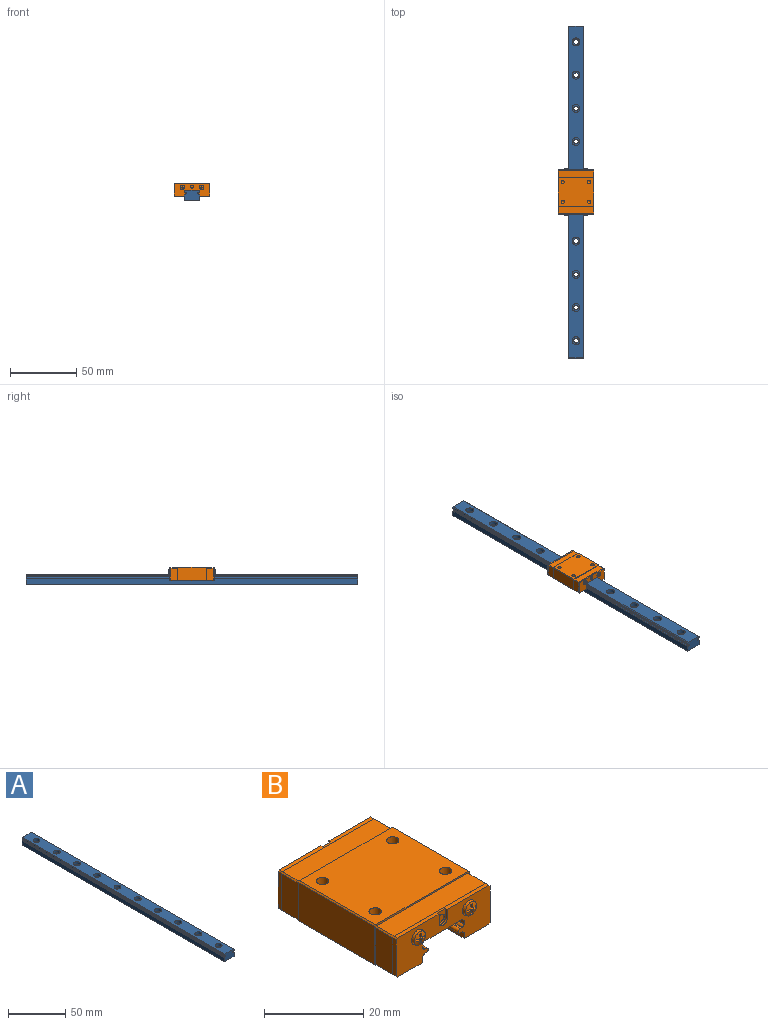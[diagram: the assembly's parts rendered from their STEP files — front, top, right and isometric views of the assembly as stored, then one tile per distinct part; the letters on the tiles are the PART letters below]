
ASSEMBLY  parts=2 mates=1
PART A: 58 faces, bbox 12x250x8 mm
  f0: cylinder r=1.75mm len=5mm, axis (0,0,1), area 55mm2, adj f11,f56
  f1: cylinder r=1.75mm len=5mm, axis (0,0,1), area 55mm2, adj f11,f54
  f2: cylinder r=1.75mm len=5mm, axis (0,0,1), area 55mm2, adj f11,f52
  f3: cylinder r=1.75mm len=5mm, axis (0,0,1), area 55mm2, adj f11,f50
  f4: cylinder r=1.75mm len=5mm, axis (0,0,1), area 55mm2, adj f11,f48
  f5: cylinder r=1.75mm len=5mm, axis (0,0,1), area 55mm2, adj f11,f46
  f6: cylinder r=1.75mm len=5mm, axis (0,0,1), area 55mm2, adj f11,f44
  f7: cylinder r=1.75mm len=5mm, axis (0,0,1), area 55mm2, adj f11,f42
  f8: cylinder r=1.75mm len=5mm, axis (0,0,1), area 55mm2, adj f11,f40
  f9: cylinder r=1.75mm len=5mm, axis (0,0,1), area 55mm2, adj f11,f38
  f10: plane 250x4.32mm, normal (-1,0,0), area 1080.5mm2, adj f11,f26,f27,f37
  f11: plane 250x12mm, normal (0,0,-1), area 2903.8mm2, adj f0,f1,f2,f3,f4,f5,f6,f7
  f12: plane 250x4.32mm, normal (1,0,0), area 1080.5mm2, adj f11,f26,f27,f30
  f13: cylinder r=1.14mm len=250mm, axis (0,1,0), area 156.5mm2, adj f26,f27,f30,f31
  f14: plane 250x0.42mm, normal (0,0,1), area 106.1mm2, adj f15,f26,f27,f31
  f15: cylinder r=0.5mm len=250mm, axis (0,1,0), area 471.3mm2, adj f14,f16,f26,f27
  f16: plane 250x0.42mm, normal (0,0,-1), area 105.2mm2, adj f15,f26,f27,f32
  f17: cylinder r=1.14mm len=250mm, axis (0,1,0), area 156.7mm2, adj f26,f27,f32,f33
  f18: plane 250x0.91mm, normal (1,0,0), area 227.5mm2, adj f26,f27,f29,f33
  f19: plane 250x11mm, normal (0,0,1), area 2467.3mm2, adj f26,f27,f28,f29,f39,f41,f43,f45
  f20: plane 250x0.91mm, normal (-1,0,0), area 227.5mm2, adj f26,f27,f28,f34
  f21: cylinder r=1.14mm len=250mm, axis (0,1,0), area 156.7mm2, adj f26,f27,f34,f35
  f22: plane 250x0.42mm, normal (0,0,-1), area 105.2mm2, adj f23,f26,f27,f35
  f23: cylinder r=0.5mm len=250mm, axis (0,1,0), area 471.3mm2, adj f22,f24,f26,f27
  f24: plane 250x0.42mm, normal (0,0,1), area 106.1mm2, adj f23,f26,f27,f36
  f25: cylinder r=1.14mm len=250mm, axis (0,1,0), area 156.5mm2, adj f26,f27,f36,f37
  f26: plane 12x8mm, normal (0,-1,0), area 91.8mm2, adj f10,f11,f12,f13,f14,f15,f16,f17
  f27: plane 12x8mm, normal (0,1,0), area 91.8mm2, adj f10,f11,f12,f13,f14,f15,f16,f17
  f28: plane 250x0.5mm, normal (-0.71,0,0.71), area 176.8mm2, adj f19,f20,f26,f27
  f29: plane 250x0.5mm, normal (0.71,0,0.71), area 176.8mm2, adj f18,f19,f26,f27
  f30: cylinder r=0.16mm len=250mm, axis (0,1,0), area 42.4mm2, adj f12,f13,f26,f27
  f31: cylinder r=0.16mm len=250mm, axis (0,1,0), area 42.4mm2, adj f13,f14,f26,f27
  f32: cylinder r=0.16mm len=250mm, axis (0,1,0), area 42.4mm2, adj f16,f17,f26,f27
  f33: cylinder r=0.16mm len=250mm, axis (0,1,0), area 42.4mm2, adj f17,f18,f26,f27
  f34: cylinder r=0.16mm len=250mm, axis (0,1,0), area 42.4mm2, adj f20,f21,f26,f27
  f35: cylinder r=0.16mm len=250mm, axis (0,1,0), area 42.4mm2, adj f21,f22,f26,f27
  f36: cylinder r=0.16mm len=250mm, axis (0,1,0), area 42.4mm2, adj f24,f25,f26,f27
  f37: cylinder r=0.16mm len=250mm, axis (0,1,0), area 42.4mm2, adj f10,f25,f26,f27
  f38: plane 6x6mm, normal (0,0,1), area 18.7mm2, adj f9,f39
  f39: cylinder r=3mm len=6mm, axis (0,0,1), area 56.5mm2, adj f19,f38
  f40: plane 6x6mm, normal (0,0,1), area 18.7mm2, adj f8,f41
  f41: cylinder r=3mm len=6mm, axis (0,0,1), area 56.5mm2, adj f19,f40
  f42: plane 6x6mm, normal (0,0,1), area 18.7mm2, adj f7,f43
  f43: cylinder r=3mm len=6mm, axis (0,0,1), area 56.5mm2, adj f19,f42
  f44: plane 6x6mm, normal (0,0,1), area 18.7mm2, adj f6,f45
  f45: cylinder r=3mm len=6mm, axis (0,0,1), area 56.5mm2, adj f19,f44
  f46: plane 6x6mm, normal (0,0,1), area 18.7mm2, adj f5,f47
  f47: cylinder r=3mm len=6mm, axis (0,0,1), area 56.5mm2, adj f19,f46
  f48: plane 6x6mm, normal (0,0,1), area 18.7mm2, adj f4,f49
  f49: cylinder r=3mm len=6mm, axis (0,0,1), area 56.5mm2, adj f19,f48
  f50: plane 6x6mm, normal (0,0,1), area 18.7mm2, adj f3,f51
  f51: cylinder r=3mm len=6mm, axis (0,0,1), area 56.5mm2, adj f19,f50
  f52: plane 6x6mm, normal (0,0,1), area 18.7mm2, adj f2,f53
  f53: cylinder r=3mm len=6mm, axis (0,0,1), area 56.5mm2, adj f19,f52
  f54: plane 6x6mm, normal (0,0,1), area 18.7mm2, adj f1,f55
  f55: cylinder r=3mm len=6mm, axis (0,0,1), area 56.5mm2, adj f19,f54
  f56: plane 6x6mm, normal (0,0,1), area 18.7mm2, adj f0,f57
  f57: cylinder r=3mm len=6mm, axis (0,0,1), area 56.5mm2, adj f19,f56
PART B: 172 faces, bbox 27x35.9x10 mm
  f0: cylinder r=1.25mm len=3.5mm, axis (0,0,-1), area 27.5mm2, adj f1,f158
  f1: cone r=0.62mm half-angle=59deg, axis (0,0,1), area 5.7mm2, adj f0
  f2: cylinder r=1.25mm len=3.5mm, axis (0,0,-1), area 27.5mm2, adj f3,f158
  f3: cone r=0.62mm half-angle=59deg, axis (0,0,1), area 5.7mm2, adj f2
  f4: cylinder r=1.25mm len=3.5mm, axis (0,0,-1), area 27.5mm2, adj f5,f158
  f5: cone r=0.62mm half-angle=59deg, axis (0,0,1), area 5.7mm2, adj f4
  f6: cylinder r=1.25mm len=3.5mm, axis (0,0,-1), area 27.5mm2, adj f7,f158
  f7: cone r=0.62mm half-angle=59deg, axis (0,0,1), area 5.7mm2, adj f6
  f8: cylinder r=0.5mm len=33.7mm, axis (0,1,0), area 63.6mm2, adj f58,f115,f148,f149
  f9: cylinder r=0.5mm len=33.7mm, axis (0,1,0), area 63.6mm2, adj f58,f115,f137,f138
  f10: cylinder r=1.15mm len=2.3mm, axis (0,1,0), area 3.6mm2, adj f114,f124
  f11: cylinder r=1.75mm len=3.5mm, axis (0,1,0), area 5.5mm2, adj f109,f115
  f12: cylinder r=1.75mm len=3.5mm, axis (0,1,0), area 5.5mm2, adj f108,f115
  f13: cone r=0.85mm half-angle=5deg, axis (0,1,0), area 11.5mm2, adj f14,f109
  f14: cone r=0.8mm half-angle=72.7deg, axis (0,1,0), area 6.3mm2, adj f13,f96,f97,f98,f99,f100,f101,f102
  f15: cone r=0.85mm half-angle=5deg, axis (0,1,0), area 11.5mm2, adj f16,f108
  f16: cone r=0.8mm half-angle=72.7deg, axis (0,1,0), area 6.3mm2, adj f15,f83,f84,f85,f86,f87,f88,f89
  f17: cylinder r=1.15mm len=2.3mm, axis (0,-1,0), area 3.6mm2, adj f57,f67
  f18: cylinder r=1.75mm len=3.5mm, axis (0,-1,0), area 5.5mm2, adj f52,f58
  f19: cylinder r=1.75mm len=3.5mm, axis (0,-1,0), area 5.5mm2, adj f51,f58
  f20: cone r=0.85mm half-angle=5deg, axis (0,-1,0), area 11.5mm2, adj f21,f52
  f21: cone r=0.8mm half-angle=72.7deg, axis (0,-1,0), area 6.3mm2, adj f20,f39,f40,f41,f42,f43,f44,f45
  f22: cone r=0.85mm half-angle=5deg, axis (0,-1,0), area 11.5mm2, adj f23,f51
  f23: cone r=0.8mm half-angle=72.7deg, axis (0,-1,0), area 6.3mm2, adj f22,f26,f27,f28,f29,f30,f31,f32
  f24: plane 26.6x9.6mm, normal (0,-1,0), area 0.3mm2, adj f55,f59,f60,f61,f62,f63,f64,f65
  f25: plane 2.4x2.4mm, normal (0,1,0), area 2.1mm2, adj f26,f27,f28,f29,f30,f31,f32,f33
  f26: plane 0.93x0.49mm, normal (0,0,1), area 0.4mm2, adj f23,f25,f29,f31
  f27: plane 0.93x0.49mm, normal (0,0,-1), area 0.4mm2, adj f23,f25,f28,f30
  f28: plane 1.36x1.29mm, normal (-1,0,0), area 1mm2, adj f23,f25,f27,f36
  f29: plane 1.36x1.29mm, normal (-1,0,0), area 1mm2, adj f23,f25,f26,f32
  f30: plane 1.36x1.29mm, normal (1,0,0), area 1mm2, adj f23,f25,f27,f33
  f31: plane 1.36x1.29mm, normal (1,0,0), area 1mm2, adj f23,f25,f26,f34
  f32: plane 1.36x1.29mm, normal (0,0,1), area 1mm2, adj f23,f25,f29,f35
  f33: plane 1.36x1.29mm, normal (0,0,-1), area 1mm2, adj f23,f25,f30,f37
  f34: plane 1.36x1.29mm, normal (0,0,1), area 1mm2, adj f23,f25,f31,f37
  f35: plane 0.93x0.49mm, normal (-1,0,0), area 0.4mm2, adj f23,f25,f32,f36
  f36: plane 1.36x1.29mm, normal (0,0,-1), area 1mm2, adj f23,f25,f28,f35
  f37: plane 0.94x0.49mm, normal (1,0,0), area 0.4mm2, adj f23,f25,f33,f34
  f38: plane 2.4x2.4mm, normal (0,1,0), area 2.1mm2, adj f39,f40,f41,f42,f43,f44,f45,f46
  f39: plane 0.93x0.49mm, normal (0,0,1), area 0.4mm2, adj f21,f38,f42,f44
  f40: plane 0.93x0.49mm, normal (0,0,-1), area 0.4mm2, adj f21,f38,f41,f43
  f41: plane 1.36x1.29mm, normal (-1,0,0), area 1mm2, adj f21,f38,f40,f49
  f42: plane 1.36x1.29mm, normal (-1,0,0), area 1mm2, adj f21,f38,f39,f45
  f43: plane 1.36x1.29mm, normal (1,0,0), area 1mm2, adj f21,f38,f40,f46
  f44: plane 1.36x1.29mm, normal (1,0,0), area 1mm2, adj f21,f38,f39,f47
  f45: plane 1.36x1.29mm, normal (0,0,1), area 1mm2, adj f21,f38,f42,f48
  f46: plane 1.36x1.29mm, normal (0,0,-1), area 1mm2, adj f21,f38,f43,f50
  f47: plane 1.36x1.29mm, normal (0,0,1), area 1mm2, adj f21,f38,f44,f50
  f48: plane 0.93x0.49mm, normal (-1,0,0), area 0.4mm2, adj f21,f38,f45,f49
  f49: plane 1.36x1.29mm, normal (0,0,-1), area 1mm2, adj f21,f38,f41,f48
  f50: plane 0.94x0.49mm, normal (1,0,0), area 0.4mm2, adj f21,f38,f46,f47
  f51: plane 3.5x3.5mm, normal (0,1,0), area 0.5mm2, adj f19,f22
  f52: plane 3.5x3.5mm, normal (0,1,0), area 0.5mm2, adj f18,f20
  f53: plane 2.1x0.5mm, normal (1,0,0), area 1.1mm2, adj f55,f56,f57,f58
  f54: plane 2.1x0.5mm, normal (-1,0,0), area 1.1mm2, adj f55,f56,f57,f58
  f55: plane 26x1mm, normal (0,0,1), area 24.8mm2, adj f24,f53,f54,f57,f58,f62,f63
  f56: cylinder r=1.2mm len=2.4mm, axis (0,-1,0), area 1.9mm2, adj f53,f54,f57,f58
  f57: plane 3.3x2.4mm, normal (0,1,0), area 3.1mm2, adj f17,f53,f54,f55,f56
  f58: plane 26.6x9.6mm, normal (0,1,0), area 172.9mm2, adj f8,f9,f18,f19,f53,f54,f55,f56
  f59: plane 7x1mm, normal (0,0,-1), area 7mm2, adj f24,f58,f65,f134
  f60: plane 7x1mm, normal (0,0,-1), area 7mm2, adj f24,f58,f66,f152
  f61: plane 9x1mm, normal (1,0,0), area 9mm2, adj f24,f58,f62,f66
  f62: plane 1x0.3mm, normal (0.71,0,0.71), area 0.4mm2, adj f24,f55,f58,f61
  f63: plane 1x0.3mm, normal (-0.71,0,0.71), area 0.4mm2, adj f24,f55,f58,f64
  f64: plane 9x1mm, normal (-1,0,0), area 9mm2, adj f24,f58,f63,f65
  f65: plane 1x0.3mm, normal (-0.71,0,-0.71), area 0.4mm2, adj f24,f58,f59,f64
  f66: plane 1x0.3mm, normal (0.71,0,-0.71), area 0.4mm2, adj f24,f58,f60,f61
  f67: plane 2.3x2.3mm, normal (0,1,0), area 4.2mm2, adj f17
  f68: cylinder r=1.14mm len=33.7mm, axis (0,-1,0), area 21.1mm2, adj f58,f115,f150,f151
  f69: cylinder r=1.14mm len=33.7mm, axis (0,-1,0), area 21.1mm2, adj f58,f115,f146,f147
  f70: cylinder r=1.14mm len=33.7mm, axis (0,-1,0), area 21.1mm2, adj f58,f115,f139,f140
  f71: cylinder r=1.14mm len=33.7mm, axis (0,-1,0), area 21.1mm2, adj f58,f115,f135,f136
  f72: plane 7x5mm, normal (0,0,-1), area 35mm2, adj f24,f79,f134,f163
  f73: plane 7x5mm, normal (0,0,-1), area 35mm2, adj f24,f80,f152,f163
  f74: plane 8.99x5mm, normal (1,0,0), area 45mm2, adj f24,f75,f80,f163
  f75: plane 5x0.3mm, normal (0.71,0,0.71), area 2.1mm2, adj f24,f74,f76,f163
  f76: plane 25.99x5mm, normal (0,0,1), area 130mm2, adj f24,f75,f77,f163
  f77: plane 5x0.3mm, normal (-0.71,0,0.71), area 2.1mm2, adj f24,f76,f78,f163
  f78: plane 8.99x5mm, normal (-1,0,0), area 45mm2, adj f24,f77,f79,f163
  f79: plane 5x0.3mm, normal (-0.71,0,-0.71), area 2.1mm2, adj f24,f72,f78,f163
  f80: plane 5x0.3mm, normal (0.71,0,-0.71), area 2.1mm2, adj f24,f73,f74,f163
  f81: plane 26.6x9.6mm, normal (0,1,0), area 0.3mm2, adj f112,f116,f117,f118,f119,f120,f121,f122
  f82: plane 2.4x2.4mm, normal (0,-1,0), area 2.1mm2, adj f83,f84,f85,f86,f87,f88,f89,f90
  f83: plane 0.93x0.49mm, normal (0,0,1), area 0.4mm2, adj f16,f82,f86,f88
  f84: plane 0.93x0.49mm, normal (0,0,-1), area 0.4mm2, adj f16,f82,f85,f87
  f85: plane 1.36x1.29mm, normal (1,0,0), area 1mm2, adj f16,f82,f84,f93
  f86: plane 1.36x1.29mm, normal (1,0,0), area 1mm2, adj f16,f82,f83,f89
  f87: plane 1.36x1.29mm, normal (-1,0,0), area 1mm2, adj f16,f82,f84,f90
  f88: plane 1.36x1.29mm, normal (-1,0,0), area 1mm2, adj f16,f82,f83,f91
  f89: plane 1.36x1.29mm, normal (0,0,1), area 1mm2, adj f16,f82,f86,f92
  f90: plane 1.36x1.29mm, normal (0,0,-1), area 1mm2, adj f16,f82,f87,f94
  f91: plane 1.36x1.29mm, normal (0,0,1), area 1mm2, adj f16,f82,f88,f94
  f92: plane 0.93x0.49mm, normal (1,0,0), area 0.4mm2, adj f16,f82,f89,f93
  f93: plane 1.36x1.29mm, normal (0,0,-1), area 1mm2, adj f16,f82,f85,f92
  f94: plane 0.94x0.49mm, normal (-1,0,0), area 0.4mm2, adj f16,f82,f90,f91
  f95: plane 2.4x2.4mm, normal (0,-1,0), area 2.1mm2, adj f96,f97,f98,f99,f100,f101,f102,f103
  f96: plane 0.93x0.49mm, normal (0,0,1), area 0.4mm2, adj f14,f95,f99,f101
  f97: plane 0.93x0.49mm, normal (0,0,-1), area 0.4mm2, adj f14,f95,f98,f100
  f98: plane 1.36x1.29mm, normal (1,0,0), area 1mm2, adj f14,f95,f97,f106
  f99: plane 1.36x1.29mm, normal (1,0,0), area 1mm2, adj f14,f95,f96,f102
  f100: plane 1.36x1.29mm, normal (-1,0,0), area 1mm2, adj f14,f95,f97,f103
  f101: plane 1.36x1.29mm, normal (-1,0,0), area 1mm2, adj f14,f95,f96,f104
  f102: plane 1.36x1.29mm, normal (0,0,1), area 1mm2, adj f14,f95,f99,f105
  f103: plane 1.36x1.29mm, normal (0,0,-1), area 1mm2, adj f14,f95,f100,f107
  f104: plane 1.36x1.29mm, normal (0,0,1), area 1mm2, adj f14,f95,f101,f107
  f105: plane 0.93x0.49mm, normal (1,0,0), area 0.4mm2, adj f14,f95,f102,f106
  f106: plane 1.36x1.29mm, normal (0,0,-1), area 1mm2, adj f14,f95,f98,f105
  f107: plane 0.94x0.49mm, normal (-1,0,0), area 0.4mm2, adj f14,f95,f103,f104
  f108: plane 3.5x3.5mm, normal (0,-1,0), area 0.5mm2, adj f12,f15
  f109: plane 3.5x3.5mm, normal (0,-1,0), area 0.5mm2, adj f11,f13
  f110: plane 2.1x0.5mm, normal (-1,0,0), area 1mm2, adj f112,f113,f114,f115
  f111: plane 2.1x0.5mm, normal (1,0,0), area 1mm2, adj f112,f113,f114,f115
  f112: plane 26x1mm, normal (0,0,1), area 24.8mm2, adj f81,f110,f111,f114,f115,f119,f120
  f113: cylinder r=1.2mm len=2.4mm, axis (0,1,0), area 1.9mm2, adj f110,f111,f114,f115
  f114: plane 3.3x2.4mm, normal (0,-1,0), area 3.1mm2, adj f10,f110,f111,f112,f113
  f115: plane 26.6x9.6mm, normal (0,-1,0), area 172.9mm2, adj f8,f9,f11,f12,f68,f69,f70,f71
  f116: plane 7x1mm, normal (0,0,-1), area 7mm2, adj f81,f115,f122,f152
  f117: plane 7x1mm, normal (0,0,-1), area 7mm2, adj f81,f115,f123,f134
  f118: plane 9x1mm, normal (-1,0,0), area 9mm2, adj f81,f115,f119,f123
  f119: plane 1x0.3mm, normal (-0.71,0,0.71), area 0.4mm2, adj f81,f112,f115,f118
  f120: plane 1x0.3mm, normal (0.71,0,0.71), area 0.4mm2, adj f81,f112,f115,f121
  f121: plane 9x1mm, normal (1,0,0), area 9mm2, adj f81,f115,f120,f122
  f122: plane 1x0.3mm, normal (0.71,0,-0.71), area 0.4mm2, adj f81,f115,f116,f121
  f123: plane 1x0.3mm, normal (-0.71,0,-0.71), area 0.4mm2, adj f81,f115,f117,f118
  f124: plane 2.3x2.3mm, normal (0,-1,0), area 4.2mm2, adj f10
  f125: plane 7x5mm, normal (0,0,-1), area 35mm2, adj f81,f132,f152,f153
  f126: plane 7x5mm, normal (0,0,-1), area 35mm2, adj f81,f133,f134,f153
  f127: plane 8.99x5mm, normal (-1,0,0), area 44.9mm2, adj f81,f128,f133,f153
  f128: plane 5x0.3mm, normal (-0.71,0,0.71), area 2.1mm2, adj f81,f127,f129,f153
  f129: plane 25.99x5mm, normal (0,0,1), area 129.9mm2, adj f81,f128,f130,f153
  f130: plane 5x0.3mm, normal (0.71,0,0.71), area 2.1mm2, adj f81,f129,f131,f153
  f131: plane 8.99x5mm, normal (1,0,0), area 45mm2, adj f81,f130,f132,f153
  f132: plane 5x0.3mm, normal (0.71,0,-0.71), area 2.1mm2, adj f81,f125,f131,f153
  f133: plane 5x0.3mm, normal (-0.71,0,-0.71), area 2.1mm2, adj f81,f126,f127,f153
  f134: plane 33.7x1.32mm, normal (1,0,0), area 44.5mm2, adj f24,f58,f59,f72,f81,f115,f117,f126
  f135: cylinder r=0.16mm len=33.7mm, axis (0,1,0), area 5.7mm2, adj f58,f71,f115,f134
  f136: cylinder r=0.16mm len=33.7mm, axis (0,1,0), area 5.7mm2, adj f58,f71,f115,f137
  f137: plane 33.7x0.42mm, normal (0,0,-1), area 14.2mm2, adj f9,f58,f115,f136
  f138: plane 33.7x0.42mm, normal (0,0,1), area 14.2mm2, adj f9,f58,f115,f139
  f139: cylinder r=0.16mm len=33.7mm, axis (0,1,0), area 5.7mm2, adj f58,f70,f115,f138
  f140: cylinder r=0.16mm len=33.7mm, axis (0,1,0), area 5.7mm2, adj f58,f70,f115,f141
  f141: plane 33.7x0.82mm, normal (1,0,0), area 27.7mm2, adj f58,f115,f140,f142
  f142: plane 33.7x0.59mm, normal (0.76,0,-0.65), area 26mm2, adj f58,f115,f141,f143
  f143: plane 33.7x11mm, normal (0,0,-1), area 370.7mm2, adj f58,f115,f142,f144
  f144: plane 33.7x0.59mm, normal (-0.76,0,-0.65), area 26mm2, adj f58,f115,f143,f145
  f145: plane 33.7x0.82mm, normal (-1,0,0), area 27.7mm2, adj f58,f115,f144,f146
  f146: cylinder r=0.16mm len=33.7mm, axis (0,1,0), area 5.7mm2, adj f58,f69,f115,f145
  f147: cylinder r=0.16mm len=33.7mm, axis (0,1,0), area 5.7mm2, adj f58,f69,f115,f148
  f148: plane 33.7x0.42mm, normal (0,0,1), area 14.2mm2, adj f8,f58,f115,f147
  f149: plane 33.7x0.42mm, normal (0,0,-1), area 14.2mm2, adj f8,f58,f115,f150
  f150: cylinder r=0.16mm len=33.7mm, axis (0,1,0), area 5.7mm2, adj f58,f68,f115,f149
  f151: cylinder r=0.16mm len=33.7mm, axis (0,1,0), area 5.7mm2, adj f58,f68,f115,f152
  f152: plane 33.7x1.32mm, normal (-1,0,0), area 44.5mm2, adj f24,f58,f60,f73,f81,f115,f116,f125
  f153: plane 27x10mm, normal (0,-1,0), area 14.9mm2, adj f125,f126,f127,f128,f129,f130,f131,f132
  f154: plane 21.7x7.2mm, normal (0,0,-1), area 156.2mm2, adj f152,f153,f161,f163
  f155: plane 21.7x7.2mm, normal (0,0,-1), area 156.2mm2, adj f134,f153,f162,f163
  f156: plane 21.7x9.4mm, normal (-1,0,0), area 204mm2, adj f153,f157,f162,f163
  f157: plane 21.7x0.3mm, normal (-0.71,0,0.71), area 9.2mm2, adj f153,f156,f158,f163
  f158: plane 26.4x21.7mm, normal (0,0,1), area 553.2mm2, adj f0,f2,f4,f6,f153,f157,f159,f163
  f159: plane 21.7x0.3mm, normal (0.71,0,0.71), area 9.2mm2, adj f153,f158,f160,f163
  f160: plane 21.7x9.4mm, normal (1,0,0), area 204mm2, adj f153,f159,f161,f163
  f161: plane 21.7x0.3mm, normal (0.71,0,-0.71), area 9.2mm2, adj f153,f154,f160,f163
  f162: plane 21.7x0.3mm, normal (-0.71,0,-0.71), area 9.2mm2, adj f153,f155,f156,f163
  f163: plane 27x10mm, normal (0,1,0), area 14.9mm2, adj f72,f73,f74,f75,f76,f77,f78,f79
  f164: cone r=0.5mm half-angle=17.1deg, axis (0,-1,0), area 2.7mm2, adj f166,f167
  f165: cylinder r=1.25mm len=2.5mm, axis (0,-1,0), area 3.9mm2, adj f166,f167
  f166: plane 2.5x2.5mm, normal (0,1,0), area 2.3mm2, adj f164,f165
  f167: plane 2.5x2.5mm, normal (0,-1,0), area 3.1mm2, adj f164,f165
  f168: cylinder r=1.25mm len=2.5mm, axis (0,-1,0), area 3.9mm2, adj f170,f171
  f169: cone r=0.5mm half-angle=17.1deg, axis (0,-1,0), area 2.7mm2, adj f170,f171
  f170: plane 2.5x2.5mm, normal (0,-1,0), area 3.1mm2, adj f168,f169
  f171: plane 2.5x2.5mm, normal (0,1,0), area 2.3mm2, adj f168,f169
PLACE A t=(35.77,149.97,-38.47)mm
PLACE B t=(29.77,8.07,-38.47)mm
MATE slider B.f8 <-> A.f15  axis (0,1,0) through (34.54,24.97,-33.02)mm
